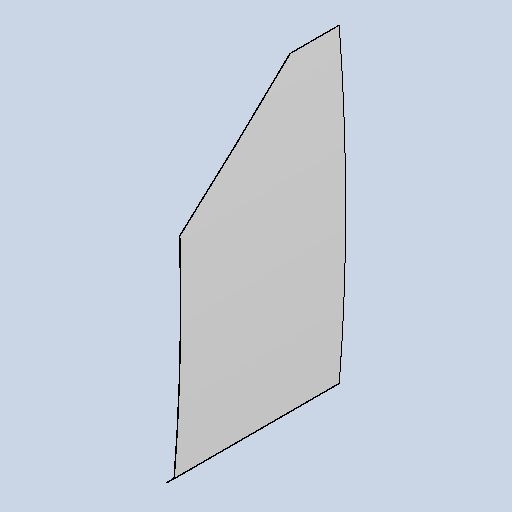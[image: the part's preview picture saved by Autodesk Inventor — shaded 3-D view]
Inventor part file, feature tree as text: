
AUTODESK INVENTOR PART (.ipt)
format: ipt  version: 2025 (Build 290162010, 162A)  size: 348,160 bytes
history: native  units: mm
features: other x4, sheet_metal_op x3, sketch x3, extrude x1
ambient origin geometry x8: Origin, YZ Plane, XZ Plane, XY Plane, X Axis, Y Axis, Z Axis, Center Point
bodies: Body1 (feature_tree)
feature tree (11):
  sheet_metal_op  "Contour Flange2"
  extrude  "Extrusion3"  Depth=3.0mm
  other  "Mark5"
  other  "A-Side Definition"
  sketch  "Sketch1"  dims[d36=3.0mm d37=3.0mm]
  other  "Plate2"
  sheet_metal_op  "Bend2"
  sheet_metal_op  "Corner2"
  sketch  "Sketch6"  dims[d38=1.5mm]
  sketch  "Sketch7"  dims[d39=6.0mm d40=3.0mm d41=980.0mm d42=3.0mm d43=3.0mm d44=12.0mm d45=3.0mm d46=3.0mm d65=6.0mm d78=3.0mm d80=3.0mm d154=5.0mm d155=63.0mm d156=11050.0mm d157=23.736478mm d159=5.0mm d160=6.981317mm d161=291.0mm d162=10.0mm d163=0.0mm d164=0.0mm d165=1843.0mm]
  other  "Definition1"
